# Revit family: ГРЕЕРС ВС-2125 + КС2
name_source: partatom
category: Оборудование
revit_build: Autodesk Revit 2017 (Build: 20161006_0315(x64)
units: mm (PartAtom-declared; Revit-internal decimal feet)

## family parameters
Общий = Нет
Основа = Грань
При загрузке вырезать с полостями = Нет
Размер круглого соединителя = Использовать диаметр
Тип детали = Нормальный
Точка расчета площади = Нет

## types (1)
- ГРЕЕРС ВС-2125 + КС2
    URL = https://greers.ru
    Вентилятор = Осевой, однофазный, переменного тока, с 3-х скоростным двигателем
    Группа модели = ГРЕЕРС ВС-2125 + КС2
    Диаметр патрубков = 20 мм
    Изготовитель = ООО "ЮНИО-ВЕНТ"
    Класс защиты = IP 54
    Классификация нагрузки = Двигатель
    Количество воды проходящей через теплообменник = 0.0 л/с
    Консоль = Да
    Коэффициент мощности = 1
    Максимальное потребление тока = 0 А
    Материал камеры смешения = Оцинкованная сталь
    Материал тепловентилятора = EPP
    Напряжение питания = 230 В
    Описание = Водяной тепловентилятор с камерой смешения
    Отметка по умолчанию = 1219 мм
    Падение давления воды в теплообменнике = 0.0 Па
    Полная установленная мощность = 0 В·А
    Производитеьность = 0.0 м³/ч
    Температура воды на входе в теплообменник = 0 °C
    Температура воды на выходе из теплообменника = 0 °C
    Температура воздуха на входе в аппарат = 0 °C
    Температура воздуха на выходе из аппарата = 0 °C
